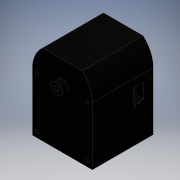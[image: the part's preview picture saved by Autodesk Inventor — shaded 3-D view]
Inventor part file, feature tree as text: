
AUTODESK INVENTOR PART (.ipt)
format: ipt  version: 2016 (Build 200138000, 138)  size: 247,808 bytes
history: native  units: mm
features: extrude x10, sketch x10, other x1
ambient origin geometry x8: Origin, YZ Plane, XZ Plane, XY Plane, X Axis, Y Axis, Z Axis, Center Point
bodies: Body1 (feature_tree)
feature tree (21):
  other  "ソリッド1"
  extrude  "押し出し1"  Depth=32.0mm
  extrude  "押し出し2"  Depth=43.0mm
  extrude  "押し出し3"  Depth=32.5mm TaperAngle=0.0deg
  extrude  "押し出し4"  Depth=9.5mm
  extrude  "押し出し5"  Depth=32.5mm TaperAngle=0.0deg
  extrude  "押し出し6"  Depth=8.5mm
  extrude  "押し出し7"  Depth=13.5mm
  extrude  "押し出し8"  Depth=2.0mm
  extrude  "押し出し9"  Depth=13.5mm
  extrude  "押し出し10"  Depth=2.0mm
  sketch  "スケッチ1"
  sketch  "スケッチ2"
  sketch  "スケッチ3"
  sketch  "スケッチ4"
  sketch  "スケッチ5"
  sketch  "スケッチ6"
  sketch  "スケッチ7"
  sketch  "スケッチ8"
  sketch  "スケッチ9"
  sketch  "スケッチ10"
